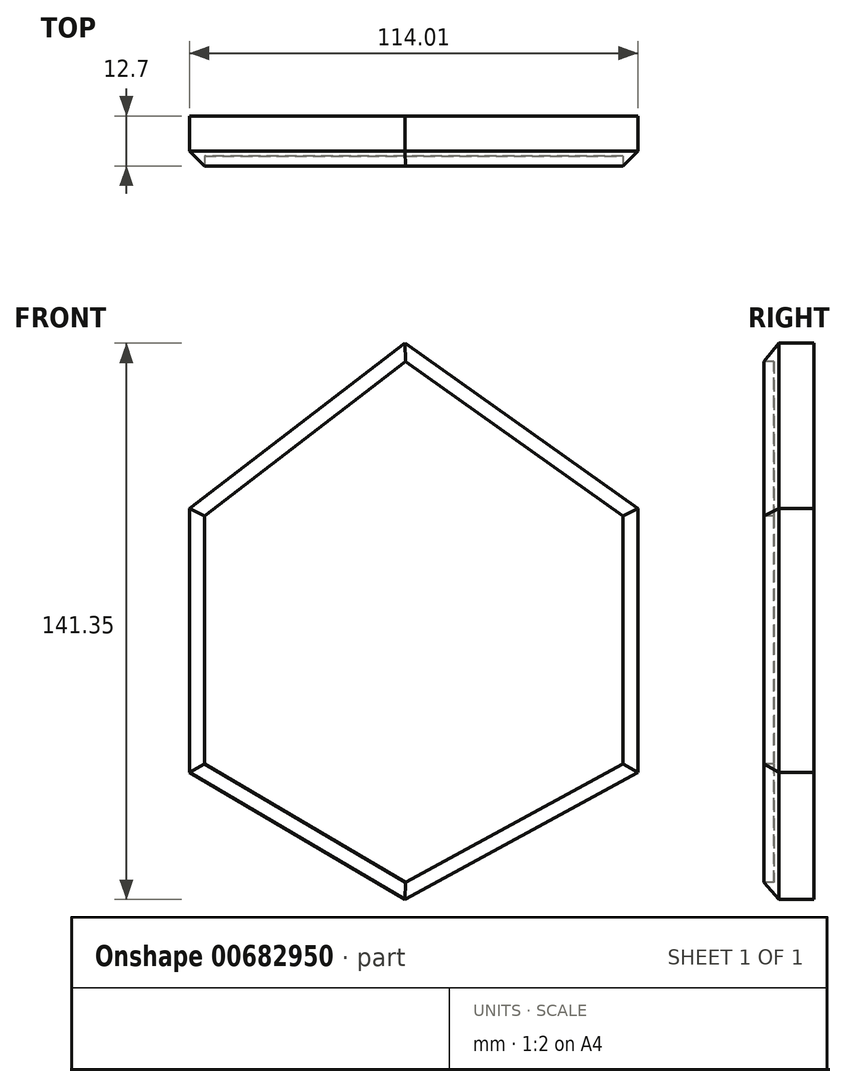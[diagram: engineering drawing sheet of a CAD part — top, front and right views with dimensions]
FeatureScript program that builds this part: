
annotation { "Feature Type Name" : "Feature", "Feature Type Description" : "" }
export const myFeature = defineFeature(function(context is Context, id is Id, definition is map)
    precondition{}
    {
        {
            var Q0;
            Q0=qCreatedBy(makeId("Front.planeOp"),FACE);
            var sketch = newSketch(context, id + "F0", { "sketchPlane" : qUnion([Q0])});
            skLineSegment(sketch, "E0", {"start": v(0, 68.56) * mm, "end": v(59.23, 26.56) * mm});
            skLineSegment(sketch, "E1", {"start": v(59.23, 26.56) * mm, "end": v(59.23, -40.56) * mm});
            skLineSegment(sketch, "E2", {"start": v(59.23, -40.56) * mm, "end": v(0, -72.79) * mm});
            skLineSegment(sketch, "E3", {"start": v(0, -72.79) * mm, "end": v(-54.78, -40.56) * mm});
            skLineSegment(sketch, "E4", {"start": v(-54.78, -40.56) * mm, "end": v(-54.78, 26.56) * mm});
            skLineSegment(sketch, "E5", {"start": v(-54.78, 26.56) * mm, "end": v(0, 68.56) * mm});
            skSolve(sketch);
        }
        {
            var Q0;
            Q0=makeQuery(id+"F0.imprint","IMPRINT",FACE,{"disambiguationData":[TD([[makeQuery(id+"F0.imprint","IMPRINT",EDGE,{"derivedFrom":sQuery(id+"F0.wireOp",EDGE,"E0")}),-1.0]])]});
            extrude(context, id + "F1", {"entities" : qUnion([Q0]), "depth" : 12.7 * mm, "offsetDistance" : 25.4 * mm});
        }
        {
            var Q0;
            Q0=makeQuery(id+"F1.opExtrude","CAP_FACE",FACE,{"disambiguationData":[OSD([sQuery(id+"F0.wireOp",EDGE,"E0"),sQuery(id+"F0.wireOp",EDGE,"E1"),sQuery(id+"F0.wireOp",EDGE,"E2"),sQuery(id+"F0.wireOp",EDGE,"E3"),sQuery(id+"F0.wireOp",EDGE,"E4"),sQuery(id+"F0.wireOp",EDGE,"E5")])],"isStart":false});
            chamfer(context, id + "F2", {"entities" : qUnion([Q0]), "width" : 3.8 * mm, "tangentPropagation" : true});
        }
        {
            var Q0;
            Q0=makeQuery(id+"F1.opExtrude","CAP_FACE",FACE,{"disambiguationData":[OSD([sQuery(id+"F0.wireOp",EDGE,"E0"),sQuery(id+"F0.wireOp",EDGE,"E1"),sQuery(id+"F0.wireOp",EDGE,"E2"),sQuery(id+"F0.wireOp",EDGE,"E3"),sQuery(id+"F0.wireOp",EDGE,"E4"),sQuery(id+"F0.wireOp",EDGE,"E5")])],"isStart":false});
            extrude(context, id + "F3", {"entities" : qUnion([Q0]), "operationType" : NewBodyOperationType.REMOVE, "oppositeDirection" : true, "depth" : 2.54 * mm, "offsetDistance" : 25.4 * mm});
        }
    });
